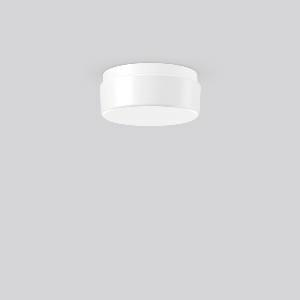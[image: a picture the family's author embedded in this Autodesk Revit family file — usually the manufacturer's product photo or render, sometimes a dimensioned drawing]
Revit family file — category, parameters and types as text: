
# Revit family: kreis_21171_002_b27d
name_source: partatom
category: Lighting Fixtures
units: mm (PartAtom-declared; Revit-internal decimal feet)

## family parameters
Cut with Voids When Loaded = No
Host = Face
Light Source = No
Part Type = Normal
Room Calculation Point = No
Round Connector Dimension = Use Diameter
Shared = No

## types (1)
- KREIS (1 x QA60/clear E27, 1320 lm, 77 W, 3000)
    Apparent Load = 77 VA
    CIE Flux Codes = 34 63 85 71 62
    Color Rendering = 90
    Color Temperature = 3000
    Default Elevation = 1800 mm
    Description = Series: KREIS
Round surface-mounted luminaire in classic design. Base: plastic. Opal glass: mouth-blown, satin finish. Diffuser fastening: spring system. Suitable for Ceiling mounting, Wall (surface). IP 43 ceiling mounting, IP 44 wall mounting. 
Colour: white
Diameter: 280 mm
Height: 120 mm
Lamp: A60
Number of lamps: 1
Wattage: 100 W
Socket: E27
System power: 75 W
Rated luminous flux: 590 lm
Luminous efficiency: 8 lm/W
Control gear: Converter not necessary
Protection class: II
Type of protection: IP 43
    Height = 120 mm
    Lamp = 1 x QA60/clear E27
    Lamp Light Flux = 1320 lm
    Lamp Power = 77 W
    Lamp count = 1
    Length = 280 mm
    Lifetime = 3000 h
    Luminous efficacy = 11 lm/W
    Manufacturer = RZB
    ModVariant = No
    Model = 21171.002
    Mounting Place = Ceiling, Wall
    Mounting Type = Surface mounted
    Number of Poles = 1
    OnlyDefault = Yes
    Power Factor = 1
    Product Name = KREIS
    Product group = Surface mounted ceiling and wall luminaires
    ProductGroupID = 305
    Protection Class = Protection class II
    Protection Degree = IP 43
    RLX_Detail_Level = 1
    RLX_Emergency_Light_Flux = 0 lm
    RLX_Emergency_Type = 0
    RLX_Emergency_Type_DB = No
    RlxData = <blob elided: 11601 chars, md5=6aa3eda3>
    Socket = E27
    Standby Power = 0 W
    System Light Flux = 815 lm
    System Power = 77 W
    Type Comments = Product without accessories
    Type Image = 21171.002.jpg
    URL = http://relux.com
    VarID = ---
    Voltage = 230 V
    Voltage Range = 220-240 V
    Weight = 0.00 kg
    Width = 0 mm  [stored 0 ft]

note: [stored X ft] marks values corroborated as IEEE doubles in the binary element streams (Revit-internal decimal feet)

## geometry (parser evidence)
native form markers: Sweep x11
no freeform markers — native parametric forms only
